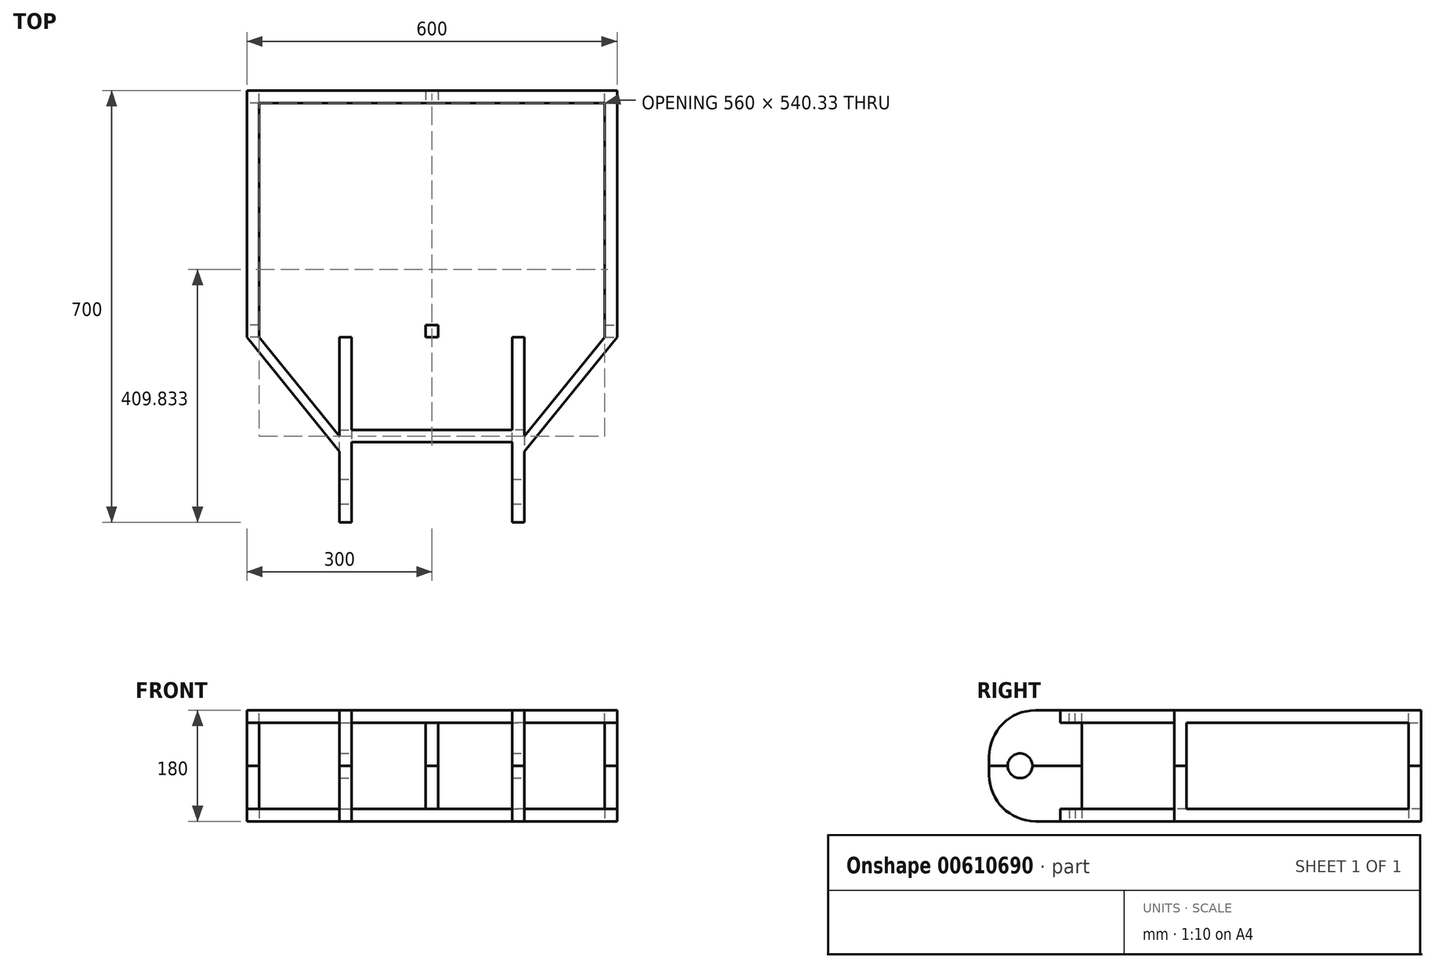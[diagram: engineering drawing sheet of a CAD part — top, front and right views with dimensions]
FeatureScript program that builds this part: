
annotation { "Feature Type Name" : "Feature", "Feature Type Description" : "" }
export const myFeature = defineFeature(function(context is Context, id is Id, definition is map)
    precondition{}
    {
        {
            var Q0;
            Q0=qCreatedBy(makeId("Top.planeOp"),FACE);
            var sketch = newSketch(context, id + "F0", { "sketchPlane" : qUnion([Q0])});
            skLineSegment(sketch, "E0.bottom", {"start": v(0, 0) * mm, "end": v(600, 0) * mm});
            skLineSegment(sketch, "E0.top", {"start": v(0, -20) * mm, "end": v(600, -20) * mm});
            skLineSegment(sketch, "E0.left", {"start": v(0, 0) * mm, "end": v(0, -20) * mm});
            skLineSegment(sketch, "E0.right", {"start": v(600, 0) * mm, "end": v(600, -20) * mm});
            skLineSegment(sketch, "E1.bottom", {"start": v(600, -20) * mm, "end": v(580, -20) * mm});
            skLineSegment(sketch, "E1.top", {"start": v(600, -400) * mm, "end": v(580, -400) * mm});
            skLineSegment(sketch, "E1.left", {"start": v(600, -20) * mm, "end": v(600, -400) * mm});
            skLineSegment(sketch, "E1.right", {"start": v(580, -20) * mm, "end": v(580, -400) * mm});
            skLineSegment(sketch, "E2.bottom", {"start": v(0, -20) * mm, "end": v(20, -20) * mm});
            skLineSegment(sketch, "E2.top", {"start": v(0, -400) * mm, "end": v(20, -400) * mm});
            skLineSegment(sketch, "E2.left", {"start": v(0, -20) * mm, "end": v(0, -400) * mm});
            skLineSegment(sketch, "E2.right", {"start": v(20, -20) * mm, "end": v(20, -400) * mm});
            skLineSegment(sketch, "E3.bottom", {"start": v(20, -400) * mm, "end": v(580, -400) * mm});
            skLineSegment(sketch, "E3.top", {"start": v(20, -380) * mm, "end": v(580, -380) * mm});
            skLineSegment(sketch, "E3.left", {"start": v(20, -400) * mm, "end": v(20, -380) * mm});
            skLineSegment(sketch, "E3.right", {"start": v(580, -400) * mm, "end": v(580, -380) * mm});
            skLineSegment(sketch, "E4.bottom", {"start": v(380, -380) * mm, "end": v(400, -380) * mm});
            skLineSegment(sketch, "E4.top", {"start": v(380, -20) * mm, "end": v(400, -20) * mm});
            skLineSegment(sketch, "E4.left", {"start": v(380, -380) * mm, "end": v(380, -20) * mm});
            skLineSegment(sketch, "E4.right", {"start": v(400, -380) * mm, "end": v(400, -20) * mm});
            skLineSegment(sketch, "E5.bottom", {"start": v(150, -400) * mm, "end": v(170, -400) * mm});
            skLineSegment(sketch, "E5.top", {"start": v(150, -700) * mm, "end": v(170, -700) * mm});
            skLineSegment(sketch, "E5.right", {"start": v(170, -400) * mm, "end": v(170, -700) * mm});
            skLineSegment(sketch, "E6.bottom", {"start": v(430, -400) * mm, "end": v(450, -400) * mm});
            skLineSegment(sketch, "E6.top", {"start": v(430, -700) * mm, "end": v(450, -700) * mm});
            skLineSegment(sketch, "E6.left", {"start": v(430, -400) * mm, "end": v(430, -700) * mm});
            skLineSegment(sketch, "E6.right", {"start": v(450, -400) * mm, "end": v(450, -700) * mm});
            skLineSegment(sketch, "E7", {"start": v(450, -585) * mm, "end": v(600, -400) * mm});
            skLineSegment(sketch, "E8", {"start": v(580, -400) * mm, "end": v(450, -560.33) * mm});
            skLineSegment(sketch, "E9", {"start": v(150, -400) * mm, "end": v(150, -700) * mm});
            skLineSegment(sketch, "E10", {"start": v(0, -400) * mm, "end": v(150, -585) * mm});
            skLineSegment(sketch, "E11", {"start": v(20, -400) * mm, "end": v(150, -560.33) * mm});
            skPoint(sketch, "E11.endSnap0", {"position": v(150, -550) * mm});
            skLineSegment(sketch, "E12.bottom", {"start": v(170, -550) * mm, "end": v(430, -550) * mm});
            skLineSegment(sketch, "E12.top", {"start": v(170, -570) * mm, "end": v(430, -570) * mm});
            skLineSegment(sketch, "E12.left", {"start": v(170, -550) * mm, "end": v(170, -570) * mm});
            skLineSegment(sketch, "E12.right", {"start": v(430, -550) * mm, "end": v(430, -570) * mm});
            skLineSegment(sketch, "E13.bottom", {"start": v(200, -380) * mm, "end": v(220, -380) * mm});
            skLineSegment(sketch, "E13.top", {"start": v(200, -20) * mm, "end": v(220, -20) * mm});
            skLineSegment(sketch, "E13.left", {"start": v(200, -380) * mm, "end": v(200, -20) * mm});
            skLineSegment(sketch, "E13.right", {"start": v(220, -380) * mm, "end": v(220, -20) * mm});
            skSolve(sketch);
        }
        {
            var Q0;
            Q0 = qSketchRegion(id + "F0", true);
            var Q1;
            Q1=makeQuery(id+"F0.imprint","IMPRINT",FACE,{"disambiguationData":[TD([[makeQuery(id+"F0.imprint","IMPRINT",EDGE,{"derivedFrom":sQuery(id+"F0.wireOp",EDGE,"E4.bottom")}),1.0]])]});
            var Q2;
            {var subQ0=sQuery(id+"F0.wireOp",EDGE,"E3.left");Q2=makeQuery(id+"F0.imprint","IMPRINT",FACE,{"disambiguationData":[TD([[makeQuery(id+"F0.imprint","IMPRINT",EDGE,{"derivedFrom":subQ0}),-1.0]])]});}
            var Q3;
            Q3=makeQuery(id+"F0.imprint","IMPRINT",FACE,{"disambiguationData":[TD([[makeQuery(id+"F0.imprint","IMPRINT",EDGE,{"derivedFrom":sQuery(id+"F0.wireOp",EDGE,"E13.bottom")}),1.0]])]});
            extrude(context, id + "F1", {"entities" : qUnion([Q0, Q1, Q2, Q3]), "depth" : 20 * mm, "offsetDistance" : 25 * mm});
        }
        {
            var Q0;
            Q0=makeQuery(id+"F1.opExtrude","CAP_FACE",FACE,{"disambiguationData":[OSD([sQuery(id+"F0.wireOp",EDGE,"E0.bottom"),sQuery(id+"F0.wireOp",EDGE,"E0.top"),sQuery(id+"F0.wireOp",EDGE,"E0.left"),sQuery(id+"F0.wireOp",EDGE,"E0.right"),sQuery(id+"F0.wireOp",EDGE,"E1.left"),sQuery(id+"F0.wireOp",EDGE,"E1.right"),sQuery(id+"F0.wireOp",EDGE,"E2.left"),sQuery(id+"F0.wireOp",EDGE,"E2.right"),sQuery(id+"F0.wireOp",EDGE,"E3.bottom"),sQuery(id+"F0.wireOp",EDGE,"E3.top"),sQuery(id+"F0.wireOp",EDGE,"E4.left"),sQuery(id+"F0.wireOp",EDGE,"E4.right"),sQuery(id+"F0.wireOp",EDGE,"E5.top"),sQuery(id+"F0.wireOp",EDGE,"E5.right"),sQuery(id+"F0.wireOp",EDGE,"E6.top"),sQuery(id+"F0.wireOp",EDGE,"E6.left"),sQuery(id+"F0.wireOp",EDGE,"E6.right"),sQuery(id+"F0.wireOp",EDGE,"E7"),sQuery(id+"F0.wireOp",EDGE,"E8"),sQuery(id+"F0.wireOp",EDGE,"E9"),sQuery(id+"F0.wireOp",EDGE,"E10"),sQuery(id+"F0.wireOp",EDGE,"E11"),sQuery(id+"F0.wireOp",EDGE,"E12.bottom"),sQuery(id+"F0.wireOp",EDGE,"E12.top")])],"isStart":false});
            var sketch = newSketch(context, id + "F2", { "sketchPlane" : qUnion([Q0])});
            skLineSegment(sketch, "E14.bottom", {"start": v(20, -20) * mm, "end": v(0, -20) * mm});
            skLineSegment(sketch, "E14.top", {"start": v(20, 0) * mm, "end": v(0, 0) * mm});
            skLineSegment(sketch, "E14.left", {"start": v(20, -20) * mm, "end": v(20, 0) * mm});
            skLineSegment(sketch, "E14.right", {"start": v(0, -20) * mm, "end": v(0, 0) * mm});
            skLineSegment(sketch, "E15.bottom", {"start": v(580, -20) * mm, "end": v(600, -20) * mm});
            skLineSegment(sketch, "E15.top", {"start": v(580, 0) * mm, "end": v(600, 0) * mm});
            skLineSegment(sketch, "E15.left", {"start": v(580, -20) * mm, "end": v(580, 0) * mm});
            skLineSegment(sketch, "E15.right", {"start": v(600, -20) * mm, "end": v(600, 0) * mm});
            skPoint(sketch, "E16.oppositeSnap0", {"position": v(490, -380) * mm});
            skLineSegment(sketch, "E16.bottom", {"start": v(580, -400) * mm, "end": v(600, -400) * mm});
            skLineSegment(sketch, "E16.top", {"start": v(580, -380) * mm, "end": v(600, -380) * mm});
            skLineSegment(sketch, "E16.left", {"start": v(580, -400) * mm, "end": v(580, -380) * mm});
            skLineSegment(sketch, "E16.right", {"start": v(600, -400) * mm, "end": v(600, -380) * mm});
            skLineSegment(sketch, "E17.bottom", {"start": v(20, -400) * mm, "end": v(0, -400) * mm});
            skLineSegment(sketch, "E17.top", {"start": v(20, -380) * mm, "end": v(0, -380) * mm});
            skLineSegment(sketch, "E17.left", {"start": v(20, -400) * mm, "end": v(20, -380) * mm});
            skLineSegment(sketch, "E17.right", {"start": v(0, -400) * mm, "end": v(0, -380) * mm});
            skLineSegment(sketch, "E18.bottom", {"start": v(150, -700) * mm, "end": v(170, -700) * mm});
            skLineSegment(sketch, "E18.top", {"start": v(150, -550) * mm, "end": v(170, -550) * mm});
            skLineSegment(sketch, "E18.left", {"start": v(150, -700) * mm, "end": v(150, -550) * mm});
            skLineSegment(sketch, "E18.right", {"start": v(170, -700) * mm, "end": v(170, -550) * mm});
            skLineSegment(sketch, "E19.bottom", {"start": v(450, -700) * mm, "end": v(430, -700) * mm});
            skLineSegment(sketch, "E19.top", {"start": v(450, -550) * mm, "end": v(430, -550) * mm});
            skLineSegment(sketch, "E19.left", {"start": v(450, -700) * mm, "end": v(450, -550) * mm});
            skLineSegment(sketch, "E19.right", {"start": v(430, -700) * mm, "end": v(430, -550) * mm});
            skLineSegment(sketch, "E20.bottom", {"start": v(290, -380) * mm, "end": v(310, -380) * mm});
            skLineSegment(sketch, "E20.top", {"start": v(290, -400) * mm, "end": v(310, -400) * mm});
            skLineSegment(sketch, "E20.left", {"start": v(290, -380) * mm, "end": v(290, -400) * mm});
            skLineSegment(sketch, "E20.right", {"start": v(310, -380) * mm, "end": v(310, -400) * mm});
            skLineSegment(sketch, "E21.bottom", {"start": v(290, 0) * mm, "end": v(310, 0) * mm});
            skLineSegment(sketch, "E21.top", {"start": v(290, -20) * mm, "end": v(310, -20) * mm});
            skLineSegment(sketch, "E21.left", {"start": v(290, 0) * mm, "end": v(290, -20) * mm});
            skLineSegment(sketch, "E21.right", {"start": v(310, 0) * mm, "end": v(310, -20) * mm});
            skSolve(sketch);
        }
        {
            var Q0;
            Q0 = qSketchRegion(id + "F2", true);
            extrude(context, id + "F3", {"entities" : qUnion([Q0]), "operationType" : NewBodyOperationType.ADD, "depth" : 70 * mm, "offsetDistance" : 25 * mm});
        }
        {
            var Q0;
            {var subQ0=sQuery(id+"F0.wireOp",EDGE,"E6.right");Q0=makeQuery(id+"F3.boolean.opBoolean","MERGE",FACE,{"derivedFrom":[makeQuery(id+"F1.opExtrude","SWEPT_FACE",FACE,{"disambiguationData":[OSD([subQ0]),TDD([makeQuery(id+"F0.imprint","IMPRINT",EDGE,{"disambiguationData":[TD([[makeQuery(id+"F0.imprint","INTERSECT",VERTEX,{"derivedFrom":[subQ0,sQuery(id+"F0.wireOp",EDGE,"E8")]}),1.0]])],"derivedFrom":subQ0})])]}),makeQuery(id+"F1.opExtrude","SWEPT_FACE",FACE,{"disambiguationData":[OSD([subQ0]),TDD([makeQuery(id+"F0.imprint","IMPRINT",EDGE,{"disambiguationData":[TD([[makeQuery(id+"F0.imprint","INTERSECT",VERTEX,{"derivedFrom":[sQuery(id+"F0.wireOp",EDGE,"E6.top"),subQ0]}),1.0]])],"derivedFrom":subQ0})])]}),makeQuery(id+"F3.opExtrude","SWEPT_FACE",FACE,{"disambiguationData":[OSD([sQuery(id+"F2.wireOp",EDGE,"E19.left")])]})]});}
            var sketch = newSketch(context, id + "F4", { "sketchPlane" : qUnion([Q0])});
            skPoint(sketch, "E22", {"position": v(-650, 90) * mm});
            skSolve(sketch);
        }
        {
            var Q0;
            Q0=sQuery(id+"F4.wireOp",VERTEX,"E22");
            var Q1;
            Q1=makeQuery(id+"F1.opExtrude","SWEPT_BODY",BODY,{"disambiguationData":[OSD([sQuery(id+"F0.wireOp",EDGE,"E0.bottom"),sQuery(id+"F0.wireOp",EDGE,"E0.top"),sQuery(id+"F0.wireOp",EDGE,"E0.left"),sQuery(id+"F0.wireOp",EDGE,"E0.right"),sQuery(id+"F0.wireOp",EDGE,"E1.left"),sQuery(id+"F0.wireOp",EDGE,"E1.right"),sQuery(id+"F0.wireOp",EDGE,"E2.left"),sQuery(id+"F0.wireOp",EDGE,"E2.right"),sQuery(id+"F0.wireOp",EDGE,"E3.bottom"),sQuery(id+"F0.wireOp",EDGE,"E3.top"),sQuery(id+"F0.wireOp",EDGE,"E4.left"),sQuery(id+"F0.wireOp",EDGE,"E4.right"),sQuery(id+"F0.wireOp",EDGE,"E5.top"),sQuery(id+"F0.wireOp",EDGE,"E5.right"),sQuery(id+"F0.wireOp",EDGE,"E6.top"),sQuery(id+"F0.wireOp",EDGE,"E6.left"),sQuery(id+"F0.wireOp",EDGE,"E6.right"),sQuery(id+"F0.wireOp",EDGE,"E7"),sQuery(id+"F0.wireOp",EDGE,"E8"),sQuery(id+"F0.wireOp",EDGE,"E9"),sQuery(id+"F0.wireOp",EDGE,"E10"),sQuery(id+"F0.wireOp",EDGE,"E11"),sQuery(id+"F0.wireOp",EDGE,"E12.bottom"),sQuery(id+"F0.wireOp",EDGE,"E12.top")])]});
            hole(context, id + "F5", {"style" : HoleStyle.SIMPLE, "endStyle" : HoleEndStyle.THROUGH, "holeDiameter" : 40 * mm, "majorDiameter" : 5 * mm, "isTappedThrough" : true, "tappedDepth" : 12 * mm, "tapClearance" : 3, "locations" : qUnion([Q0]), "scope" : qUnion([Q1])});
        }
        {
            var Q0;
            Q0=makeQuery(id+"F1.opExtrude","CAP_EDGE",EDGE,{"disambiguationData":[OSD([sQuery(id+"F0.wireOp",EDGE,"E5.top")])],"isStart":true});
            var Q1;
            Q1=makeQuery(id+"F1.opExtrude","CAP_EDGE",EDGE,{"disambiguationData":[OSD([sQuery(id+"F0.wireOp",EDGE,"E6.top")])],"isStart":true});
            fillet(context, id + "F6", {"entities" : qUnion([Q0, Q1]), "radius" : 75 * mm, "tangentPropagation" : true, "allowEdgeOverflow" : false});
        }
        {
            var Q0;
            Q0=makeQuery(id+"F1.opExtrude","SWEPT_BODY",BODY,{"disambiguationData":[OSD([sQuery(id+"F0.wireOp",EDGE,"E0.bottom"),sQuery(id+"F0.wireOp",EDGE,"E0.top"),sQuery(id+"F0.wireOp",EDGE,"E0.left"),sQuery(id+"F0.wireOp",EDGE,"E0.right"),sQuery(id+"F0.wireOp",EDGE,"E1.left"),sQuery(id+"F0.wireOp",EDGE,"E1.right"),sQuery(id+"F0.wireOp",EDGE,"E2.left"),sQuery(id+"F0.wireOp",EDGE,"E2.right"),sQuery(id+"F0.wireOp",EDGE,"E3.bottom"),sQuery(id+"F0.wireOp",EDGE,"E3.top"),sQuery(id+"F0.wireOp",EDGE,"E4.left"),sQuery(id+"F0.wireOp",EDGE,"E4.right"),sQuery(id+"F0.wireOp",EDGE,"E5.top"),sQuery(id+"F0.wireOp",EDGE,"E5.right"),sQuery(id+"F0.wireOp",EDGE,"E6.top"),sQuery(id+"F0.wireOp",EDGE,"E6.left"),sQuery(id+"F0.wireOp",EDGE,"E6.right"),sQuery(id+"F0.wireOp",EDGE,"E7"),sQuery(id+"F0.wireOp",EDGE,"E8"),sQuery(id+"F0.wireOp",EDGE,"E9"),sQuery(id+"F0.wireOp",EDGE,"E10"),sQuery(id+"F0.wireOp",EDGE,"E11"),sQuery(id+"F0.wireOp",EDGE,"E12.bottom"),sQuery(id+"F0.wireOp",EDGE,"E12.top")])]});
            var Q1;
            {var subQ0=sQuery(id+"F2.wireOp",EDGE,"E18.top");var subQ4=sQuery(id+"F2.wireOp",EDGE,"E18.left");var subQ5=sQuery(id+"F2.wireOp",EDGE,"E18.right");Q1=makeQuery(id+"F5.hole-0.boolean.opBoolean","SPLIT",FACE,{"disambiguationData":[TD([makeQuery(id+"F3.opExtrude","SWEPT_FACE",FACE,{"disambiguationData":[OSD([subQ0])]})])],"derivedFrom":makeQuery(id+"F3.opExtrude","CAP_FACE",FACE,{"disambiguationData":[OSD([sQuery(id+"F2.wireOp",EDGE,"E18.bottom"),subQ0,subQ4,subQ5])],"isStart":false})});}
            mirror(context, id + "F7", {"operationType" : NewBodyOperationType.ADD, "entities" : qUnion([Q0]), "mirrorPlane" : qUnion([Q1])});
        }
    });
